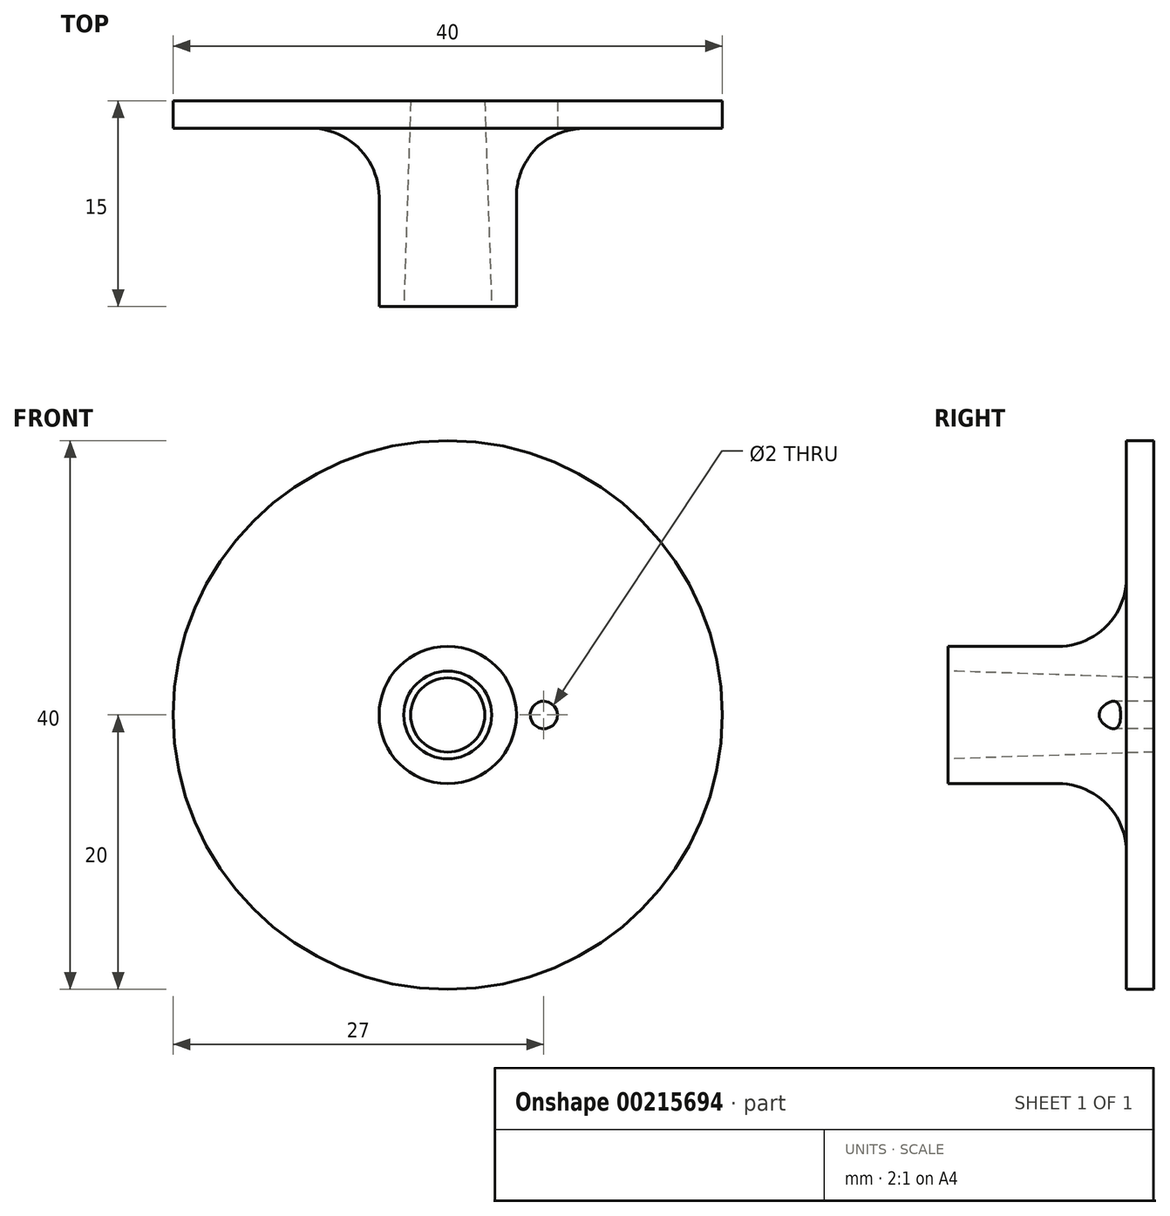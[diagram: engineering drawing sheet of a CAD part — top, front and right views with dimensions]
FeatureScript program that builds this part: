
annotation { "Feature Type Name" : "Feature", "Feature Type Description" : "" }
export const myFeature = defineFeature(function(context is Context, id is Id, definition is map)
    precondition{}
    {
        {
            var Q0;
            Q0=qCreatedBy(makeId("Top.planeOp"),FACE);
            var sketch = newSketch(context, id + "F0", { "sketchPlane" : qUnion([Q0])});
            skLineSegment(sketch, "E0", {"start": v(0, 15.22) * mm, "end": v(0, -16.41) * mm, "construction": true});
            skLineSegment(sketch, "E1", {"start": v(-3.2, 0) * mm, "end": v(-2.7, 15) * mm});
            skLineSegment(sketch, "E2", {"start": v(-2.7, 15) * mm, "end": v(-20, 15) * mm});
            skLineSegment(sketch, "E3", {"start": v(-20, 15) * mm, "end": v(-20, 13) * mm});
            skLineSegment(sketch, "E4", {"start": v(-20, 13) * mm, "end": v(-5, 13) * mm});
            skLineSegment(sketch, "E5", {"start": v(-5, 13) * mm, "end": v(-5, 0) * mm});
            skLineSegment(sketch, "E6", {"start": v(-5, 0) * mm, "end": v(-3.2, 0) * mm});
            skSolve(sketch);
        }
        {
            var Q0;
            Q0 = qSketchRegion(id + "F0", true);
            var Q1;
            Q1=sQuery(id+"F0.wireOp",EDGE,"E0");
            revolve(context, id + "F1", {"entities" : qUnion([Q0]), "axis" : qUnion([Q1]), "revolveType" : RevolveType.FULL});
        }
        {
            var Q0;
            Q0=makeQuery(id+"F1.opRevolve","SWEPT_EDGE",EDGE,{"disambiguationData":[OSD([sQuery(id+"F0.wireOp",EDGE,"E4"),sQuery(id+"F0.wireOp",EDGE,"E5")])]});
            fillet(context, id + "F2", {"entities" : qUnion([Q0]), "radius" : 5 * mm, "tangentPropagation" : true, "allowEdgeOverflow" : false});
        }
        {
            var Q0;
            Q0=makeQuery(id+"F1.opRevolve","SWEPT_FACE",FACE,{"disambiguationData":[OSD([sQuery(id+"F0.wireOp",EDGE,"E4")])]});
            var sketch = newSketch(context, id + "F3", { "sketchPlane" : qUnion([Q0])});
            skCircle(sketch, "E7", {"center": v(7, 0) * mm, "radius": 1 * mm});
            skSolve(sketch);
        }
        {
            var Q0;
            Q0 = qSketchRegion(id + "F3", true);
            extrude(context, id + "F4", {"entities" : qUnion([Q0]), "operationType" : NewBodyOperationType.REMOVE, "endBound" : BoundingType.THROUGH_ALL, "oppositeDirection" : true, "depth" : 25 * mm, "hasSecondDirection" : true, "secondDirectionBound" : SecondDirectionBoundingType.THROUGH_ALL, "secondDirectionOppositeDirection" : false, "secondDirectionDepth" : 25 * mm});
        }
    });
